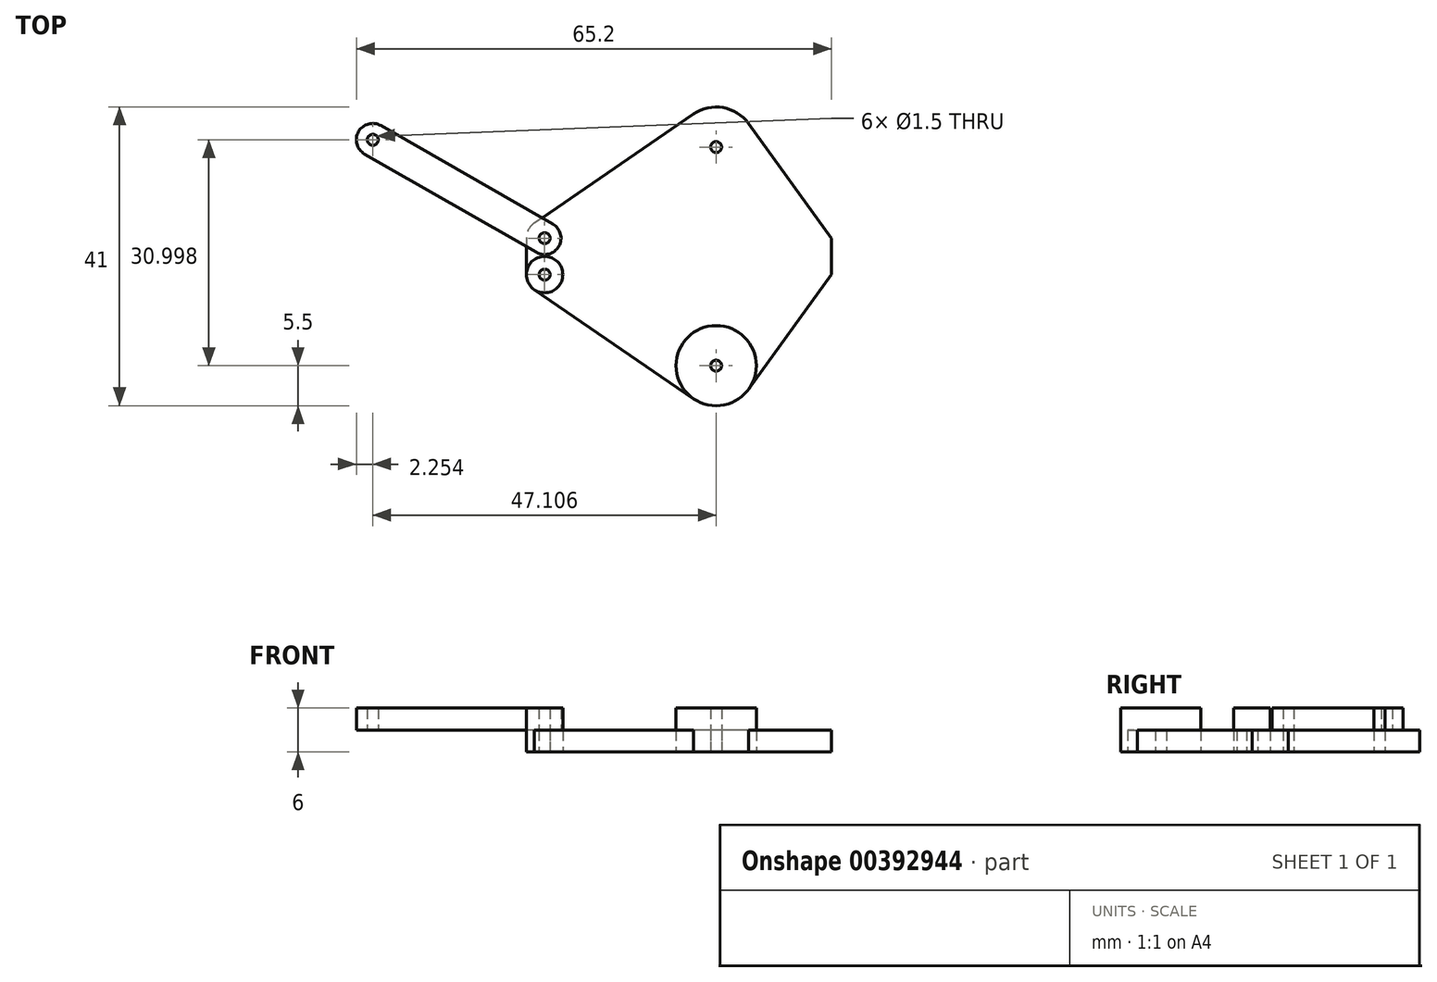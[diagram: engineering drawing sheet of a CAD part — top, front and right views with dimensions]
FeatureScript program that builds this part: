
annotation { "Feature Type Name" : "Feature", "Feature Type Description" : "" }
export const myFeature = defineFeature(function(context is Context, id is Id, definition is map)
    precondition{}
    {
        {
            var Q0;
            Q0=qCreatedBy(makeId("Top.planeOp"),FACE);
            var sketch = newSketch(context, id + "F0", { "sketchPlane" : qUnion([Q0])});
            skCircle(sketch, "E0", {"center": v(0, 15) * mm, "radius": 5.5 * mm});
            skCircle(sketch, "E1", {"center": v(-23.54, 2.5) * mm, "radius": 2.5 * mm});
            skLineSegment(sketch, "E2", {"start": v(-23.54, 0) * mm, "end": v(15.84, 0) * mm});
            skLineSegment(sketch, "E3", {"start": v(15.84, 0) * mm, "end": v(15.84, 2.5) * mm});
            skLineSegment(sketch, "E4", {"start": v(15.84, 2.5) * mm, "end": v(4.45, 18.23) * mm});
            skLineSegment(sketch, "E5", {"start": v(-3.11, 19.54) * mm, "end": v(-24.95, 4.56) * mm});
            skLineSegment(sketch, "E6.MirrorCS", {"start": v(15.84, 0) * mm, "end": v(15.84, -2.5) * mm});
            skLineSegment(sketch, "E7.MirrorCS", {"start": v(15.84, -2.5) * mm, "end": v(4.45, -18.23) * mm});
            skCircle(sketch, "E8.MirrorC", {"center": v(-23.54, -2.5) * mm, "radius": 2.5 * mm});
            skLineSegment(sketch, "E9.MirrorCS", {"start": v(-3.11, -19.54) * mm, "end": v(-24.95, -4.56) * mm});
            skCircle(sketch, "E10.MirrorC", {"center": v(0, -15) * mm, "radius": 5.5 * mm});
            skLineSegment(sketch, "E11", {"start": v(-26.04, 2.5) * mm, "end": v(-26.04, -2.5) * mm});
            skCircle(sketch, "E12", {"center": v(0, 15) * mm, "radius": 0.75 * mm});
            skCircle(sketch, "E13", {"center": v(-23.54, 2.5) * mm, "radius": 0.75 * mm});
            skCircle(sketch, "E14.MirrorC", {"center": v(-23.54, -2.5) * mm, "radius": 0.75 * mm});
            skCircle(sketch, "E15.MirrorC", {"center": v(0, -15) * mm, "radius": 0.75 * mm});
            skSolve(sketch);
        }
        {
            var Q0;
            Q0=makeQuery(id+"F0.imprint","IMPRINT",FACE,{"disambiguationData":[TD([[makeQuery(id+"F0.imprint","IMPRINT",EDGE,{"derivedFrom":sQuery(id+"F0.wireOp",EDGE,"E3")}),1.0]])]});
            var Q1;
            Q1=makeQuery(id+"F0.imprint","IMPRINT",FACE,{"disambiguationData":[TD([[makeQuery(id+"F0.imprint","IMPRINT",EDGE,{"derivedFrom":sQuery(id+"F0.wireOp",EDGE,"E12")}),-1.0]])]});
            var Q2;
            Q2=makeQuery(id+"F0.imprint","IMPRINT",FACE,{"disambiguationData":[TD([[makeQuery(id+"F0.imprint","IMPRINT",EDGE,{"derivedFrom":sQuery(id+"F0.wireOp",EDGE,"E13")}),-1.0]])]});
            var Q3;
            {var subQ3=sQuery(id+"F0.wireOp",EDGE,"E11");Q3=makeQuery(id+"F0.imprint","IMPRINT",FACE,{"disambiguationData":[TD([[makeQuery(id+"F0.imprint","IMPRINT",EDGE,{"derivedFrom":subQ3}),1.0]])]});}
            var Q4;
            Q4=makeQuery(id+"F0.imprint","IMPRINT",FACE,{"disambiguationData":[TD([[makeQuery(id+"F0.imprint","IMPRINT",EDGE,{"derivedFrom":sQuery(id+"F0.wireOp",EDGE,"E6.MirrorCS")}),-1.0]])]});
            var Q5;
            Q5=makeQuery(id+"F0.imprint","IMPRINT",FACE,{"disambiguationData":[TD([[makeQuery(id+"F0.imprint","IMPRINT",EDGE,{"derivedFrom":sQuery(id+"F0.wireOp",EDGE,"E15.MirrorC")}),1.0]])]});
            var Q6;
            Q6=makeQuery(id+"F0.imprint","IMPRINT",FACE,{"disambiguationData":[TD([[makeQuery(id+"F0.imprint","IMPRINT",EDGE,{"derivedFrom":sQuery(id+"F0.wireOp",EDGE,"E14.MirrorC")}),1.0]])]});
            extrude(context, id + "F1", {"entities" : qUnion([Q0, Q1, Q2, Q3, Q4, Q5, Q6]), "depth" : 3 * mm});
        }
        {
            var Q0;
            Q0=makeQuery(id+"F0.imprint","IMPRINT",FACE,{"disambiguationData":[TD([[makeQuery(id+"F0.imprint","IMPRINT",EDGE,{"derivedFrom":sQuery(id+"F0.wireOp",EDGE,"E12")}),1.0]])]});
            var Q1;
            Q1=makeQuery(id+"F0.imprint","IMPRINT",FACE,{"disambiguationData":[TD([[makeQuery(id+"F0.imprint","IMPRINT",EDGE,{"derivedFrom":sQuery(id+"F0.wireOp",EDGE,"E13")}),1.0]])]});
            var Q2;
            Q2=makeQuery(id+"F0.imprint","IMPRINT",FACE,{"disambiguationData":[TD([[makeQuery(id+"F0.imprint","IMPRINT",EDGE,{"derivedFrom":sQuery(id+"F0.wireOp",EDGE,"E14.MirrorC")}),-1.0]])]});
            var Q3;
            Q3=makeQuery(id+"F0.imprint","IMPRINT",FACE,{"disambiguationData":[TD([[makeQuery(id+"F0.imprint","IMPRINT",EDGE,{"derivedFrom":sQuery(id+"F0.wireOp",EDGE,"E15.MirrorC")}),-1.0]])]});
            extrude(context, id + "F2", {"entities" : qUnion([Q0, Q1, Q2, Q3]), "depth" : 6 * mm});
        }
        {
            var Q0;
            Q0=makeQuery(id+"F1.opExtrude","CAP_FACE",FACE,{"disambiguationData":[OSD([sQuery(id+"F0.wireOp",EDGE,"E0"),sQuery(id+"F0.wireOp",EDGE,"E1"),sQuery(id+"F0.wireOp",EDGE,"E3"),sQuery(id+"F0.wireOp",EDGE,"E4"),sQuery(id+"F0.wireOp",EDGE,"E5"),sQuery(id+"F0.wireOp",EDGE,"E6.MirrorCS"),sQuery(id+"F0.wireOp",EDGE,"E7.MirrorCS"),sQuery(id+"F0.wireOp",EDGE,"E8.MirrorC"),sQuery(id+"F0.wireOp",EDGE,"E9.MirrorCS"),sQuery(id+"F0.wireOp",EDGE,"E10.MirrorC"),sQuery(id+"F0.wireOp",EDGE,"E11"),sQuery(id+"F0.wireOp",EDGE,"E12"),sQuery(id+"F0.wireOp",EDGE,"E13"),sQuery(id+"F0.wireOp",EDGE,"E14.MirrorC"),sQuery(id+"F0.wireOp",EDGE,"E15.MirrorC")])],"isStart":false});
            var sketch = newSketch(context, id + "F3", { "sketchPlane" : qUnion([Q0])});
            skArc(sketch, "E16", {"start": v(-24.65, 0.55) * mm, "mid": v(-21.58, 1.38) * mm, "end": v(-22.42, 4.45) * mm});
            skLineSegment(sketch, "E17", {"start": v(-24.65, 0.55) * mm, "end": v(-48.22, 14.05) * mm});
            skLineSegment(sketch, "E18", {"start": v(-45.99, 17.95) * mm, "end": v(-22.42, 4.45) * mm});
            skArc(sketch, "E19", {"start": v(-45.99, 17.95) * mm, "mid": v(-49.06, 17.12) * mm, "end": v(-48.22, 14.05) * mm});
            skCircle(sketch, "E20", {"center": v(-47.1, 16) * mm, "radius": 0.75 * mm});
            skCircle(sketch, "E21", {"center": v(-23.54, 2.5) * mm, "radius": 0.75 * mm});
            skSolve(sketch);
        }
        {
            var Q0;
            {var subQ1=sQuery(id+"F3.wireOp",EDGE,"E16");Q0=makeQuery(id+"F3.imprint","IMPRINT",FACE,{"disambiguationData":[TD([[makeQuery(id+"F3.imprint","IMPRINT",EDGE,{"derivedFrom":subQ1}),1.0]])]});}
            var Q1;
            {var subQ0=sQuery(id+"F3.wireOp",EDGE,"E19");Q1=makeQuery(id+"F3.imprint","IMPRINT",FACE,{"disambiguationData":[TD([[makeQuery(id+"F3.imprint","IMPRINT",EDGE,{"derivedFrom":subQ0}),1.0]])]});}
            extrude(context, id + "F4", {"entities" : qUnion([Q0, Q1]), "depth" : 3 * mm});
        }
    });
